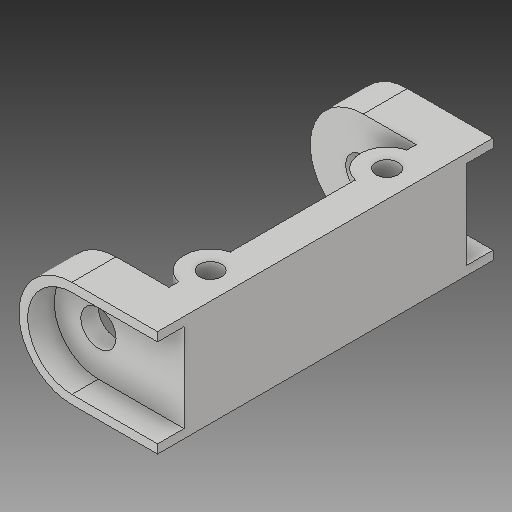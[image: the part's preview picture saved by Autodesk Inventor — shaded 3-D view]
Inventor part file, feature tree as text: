
AUTODESK INVENTOR PART (.ipt)
format: ipt  version: 2019 (Build 230136000, 136)  size: 177,152 bytes
history: native  units: in
note: dims shown in document units (in); Inventor stores cm internally (conversion verified against a paired STEP export)
features: reference x7, extrude x5, sketch x5, other x4, mirror x1, projected_geometry x1
ambient origin geometry x8: Origin, YZ Plane, XZ Plane, XY Plane, X Axis, Y Axis, Z Axis, Center Point
bodies: Solid1 (feature_tree)
feature tree (23):
  extrude  "Extrusion1"  Depth=0.05in
  extrude  "Extrusion2"  Depth=1.9in TaperAngle=0.0deg
  extrude  "Extrusion3"  Depth=1.9in
  extrude  "Extrusion4"  Depth=0.05in
  extrude  "Extrusion5"  Depth=1.4in
  mirror  "Mirror1"
  sketch  "Sketch1"  dims[d0=0.05in d1=0.785in]
  reference  "Reference1"
  reference  "Reference2"
  reference  "Reference3"
  sketch  "Sketch2"  dims[d2=1.9in d3=0.0in d4=1.9in d5=0.0in]
  reference  "Reference4"
  reference  "Reference5"
  sketch  "Sketch3"  dims[d9=1.9in d10=0.0in d11=0.2in]
  reference  "Reference6"
  reference  "Reference7"
  sketch  "Sketch4"  dims[d12=1.7in d13=0.0in d14=0.05in]
  sketch  "Sketch5"  dims[d15=0.15in d16=0.0in d17=1.4in d18=0.6in]
  projected_geometry  "Projected Loop1"
  other  "<userpath>\OneDrive\Documents\Inventor\Mr.Green\Front_Wheel_Drive.iam"
  other  "Front_Wheel_Drive.iam"
  other  "A_Arm:1"
  other  "A_Arm_MIR:1"
